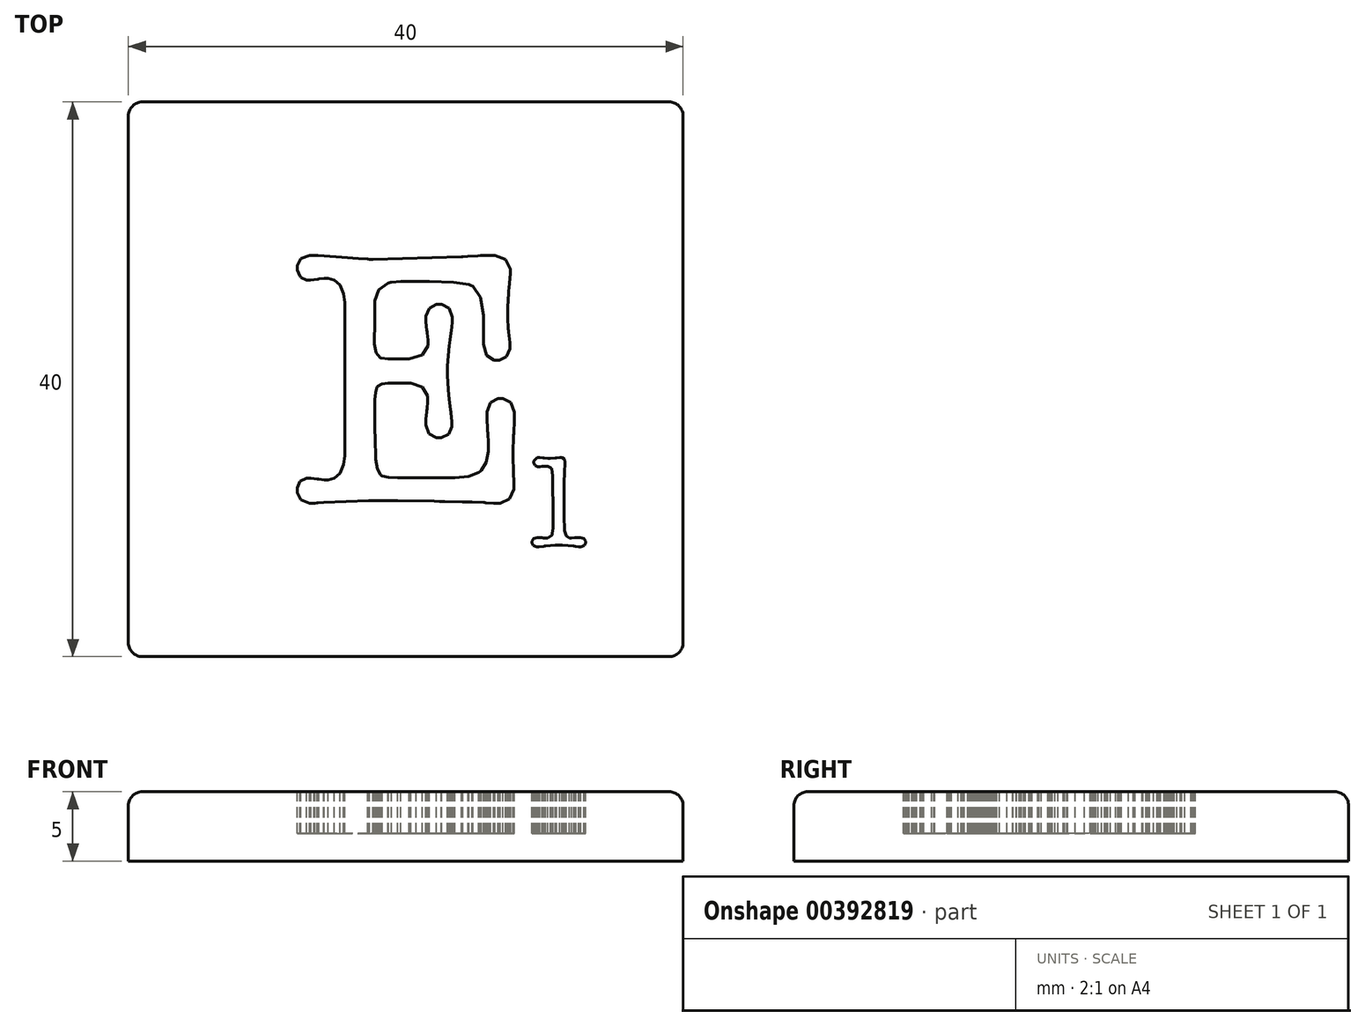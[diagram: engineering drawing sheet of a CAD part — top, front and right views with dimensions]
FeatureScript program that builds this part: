
annotation { "Feature Type Name" : "Feature", "Feature Type Description" : "" }
export const myFeature = defineFeature(function(context is Context, id is Id, definition is map)
    precondition{}
    {
        {
            var Q0;
            Q0=qCreatedBy(makeId("Top.planeOp"),FACE);
            var sketch = newSketch(context, id + "F0", { "sketchPlane" : qUnion([Q0])});
            skLineSegment(sketch, "E0.bottom", {"start": v(20, -20) * mm, "end": v(-20, -20) * mm});
            skLineSegment(sketch, "E0.top", {"start": v(20, 20) * mm, "end": v(-20, 20) * mm});
            skLineSegment(sketch, "E0.left", {"start": v(20, -20) * mm, "end": v(20, 20) * mm});
            skLineSegment(sketch, "E0.right", {"start": v(-20, -20) * mm, "end": v(-20, 20) * mm});
            skPoint(sketch, "E0.middle", {"position": v(0, 0) * mm});
            skSolve(sketch);
        }
        {
            var Q0;
            Q0=makeQuery(id+"F0.imprint","IMPRINT",FACE,{"disambiguationData":[TD([[makeQuery(id+"F0.imprint","IMPRINT",EDGE,{"derivedFrom":sQuery(id+"F0.wireOp",EDGE,"E0.bottom")}),-1.0]])]});
            extrude(context, id + "F1", {"entities" : qUnion([Q0]), "depth" : -5 * mm});
        }
        {
            var Q0;
            Q0=makeQuery(id+"F1.opExtrude","CAP_FACE",FACE,{"disambiguationData":[OSD([sQuery(id+"F0.wireOp",EDGE,"E0.bottom"),sQuery(id+"F0.wireOp",EDGE,"E0.top"),sQuery(id+"F0.wireOp",EDGE,"E0.left"),sQuery(id+"F0.wireOp",EDGE,"E0.right")])],"isStart":true});
            var Q1;
            Q1=makeQuery(id+"F1.opExtrude","SWEPT_EDGE",EDGE,{"disambiguationData":[OSD([sQuery(id+"F0.wireOp",EDGE,"E0.top"),sQuery(id+"F0.wireOp",EDGE,"E0.right")])]});
            var Q2;
            Q2=makeQuery(id+"F1.opExtrude","SWEPT_EDGE",EDGE,{"disambiguationData":[OSD([sQuery(id+"F0.wireOp",EDGE,"E0.top"),sQuery(id+"F0.wireOp",EDGE,"E0.left")])]});
            var Q3;
            Q3=makeQuery(id+"F1.opExtrude","SWEPT_EDGE",EDGE,{"disambiguationData":[OSD([sQuery(id+"F0.wireOp",EDGE,"E0.bottom"),sQuery(id+"F0.wireOp",EDGE,"E0.right")])]});
            var Q4;
            Q4=makeQuery(id+"F1.opExtrude","SWEPT_EDGE",EDGE,{"disambiguationData":[OSD([sQuery(id+"F0.wireOp",EDGE,"E0.bottom"),sQuery(id+"F0.wireOp",EDGE,"E0.left")])]});
            fillet(context, id + "F2", {"entities" : qUnion([Q0, Q1, Q2, Q3, Q4]), "radius" : 1 * mm, "tangentPropagation" : true, "allowEdgeOverflow" : false});
        }
        {
            var Q0;
            Q0=qCreatedBy(makeId("Top.planeOp"),FACE);
            var sketch = newSketch(context, id + "F3", { "sketchPlane" : qUnion([Q0])});
            skLineSegment(sketch, "E1", {"start": v(-4.4, 5.32) * mm, "end": v(-4.4, 5.53) * mm});
            skLineSegment(sketch, "E2", {"start": v(-4.4, 5.53) * mm, "end": v(-4.48, 6.18) * mm});
            skLineSegment(sketch, "E3", {"start": v(-4.48, 6.18) * mm, "end": v(-4.73, 6.79) * mm});
            skLineSegment(sketch, "E4", {"start": v(-4.73, 6.79) * mm, "end": v(-5.15, 7.16) * mm});
            skLineSegment(sketch, "E5", {"start": v(-5.15, 7.16) * mm, "end": v(-5.6, 7.28) * mm});
            skLineSegment(sketch, "E6", {"start": v(-5.6, 7.28) * mm, "end": v(-5.74, 7.28) * mm});
            skLineSegment(sketch, "E7", {"start": v(-5.74, 7.28) * mm, "end": v(-5.88, 7.28) * mm});
            skLineSegment(sketch, "E8", {"start": v(-5.88, 7.28) * mm, "end": v(-6.27, 7.23) * mm});
            skLineSegment(sketch, "E9", {"start": v(-6.27, 7.23) * mm, "end": v(-6.3, 7.22) * mm});
            skLineSegment(sketch, "E10", {"start": v(-6.3, 7.22) * mm, "end": v(-6.37, 7.21) * mm});
            skLineSegment(sketch, "E11", {"start": v(-6.37, 7.21) * mm, "end": v(-6.85, 7.14) * mm});
            skLineSegment(sketch, "E12", {"start": v(-6.85, 7.14) * mm, "end": v(-7.01, 7.14) * mm});
            skLineSegment(sketch, "E13", {"start": v(-7.01, 7.14) * mm, "end": v(-7.16, 7.14) * mm});
            skLineSegment(sketch, "E14", {"start": v(-7.16, 7.14) * mm, "end": v(-7.55, 7.35) * mm});
            skLineSegment(sketch, "E15", {"start": v(-7.55, 7.35) * mm, "end": v(-7.6, 7.4) * mm});
            skLineSegment(sketch, "E16", {"start": v(-7.6, 7.4) * mm, "end": v(-7.63, 7.44) * mm});
            skLineSegment(sketch, "E17", {"start": v(-7.63, 7.44) * mm, "end": v(-7.83, 7.87) * mm});
            skLineSegment(sketch, "E18", {"start": v(-7.83, 7.87) * mm, "end": v(-7.83, 8.02) * mm});
            skLineSegment(sketch, "E19", {"start": v(-7.83, 8.02) * mm, "end": v(-7.83, 8.2) * mm});
            skLineSegment(sketch, "E20", {"start": v(-7.83, 8.2) * mm, "end": v(-7.55, 8.71) * mm});
            skLineSegment(sketch, "E21", {"start": v(-7.55, 8.71) * mm, "end": v(-6.93, 8.94) * mm});
            skLineSegment(sketch, "E22", {"start": v(-6.93, 8.94) * mm, "end": v(-6.72, 8.94) * mm});
            skLineSegment(sketch, "E23", {"start": v(-6.72, 8.94) * mm, "end": v(-6.62, 8.94) * mm});
            skLineSegment(sketch, "E24", {"start": v(-6.62, 8.94) * mm, "end": v(-6.39, 8.92) * mm});
            skLineSegment(sketch, "E25", {"start": v(-6.39, 8.92) * mm, "end": v(-6.32, 8.92) * mm});
            skLineSegment(sketch, "E26", {"start": v(-6.32, 8.92) * mm, "end": v(-5.9, 8.89) * mm});
            skLineSegment(sketch, "E27", {"start": v(-5.9, 8.89) * mm, "end": v(-4.6, 8.8) * mm});
            skLineSegment(sketch, "E28", {"start": v(-4.6, 8.8) * mm, "end": v(-3.41, 8.72) * mm});
            skLineSegment(sketch, "E29", {"start": v(-3.41, 8.72) * mm, "end": v(-2.75, 8.67) * mm});
            skLineSegment(sketch, "E30", {"start": v(-2.75, 8.67) * mm, "end": v(-2.62, 8.65) * mm});
            skLineSegment(sketch, "E31", {"start": v(-2.62, 8.65) * mm, "end": v(-2.36, 8.65) * mm});
            skLineSegment(sketch, "E32", {"start": v(-2.36, 8.65) * mm, "end": v(4.02, 8.84) * mm});
            skLineSegment(sketch, "E33", {"start": v(4.02, 8.84) * mm, "end": v(4.13, 8.84) * mm});
            skLineSegment(sketch, "E34", {"start": v(4.13, 8.84) * mm, "end": v(4.46, 8.86) * mm});
            skLineSegment(sketch, "E35", {"start": v(4.46, 8.86) * mm, "end": v(5.2, 8.9) * mm});
            skLineSegment(sketch, "E36", {"start": v(5.2, 8.9) * mm, "end": v(5.4, 8.92) * mm});
            skLineSegment(sketch, "E37", {"start": v(5.4, 8.92) * mm, "end": v(5.47, 8.92) * mm});
            skLineSegment(sketch, "E38", {"start": v(5.47, 8.92) * mm, "end": v(6, 8.94) * mm});
            skLineSegment(sketch, "E39", {"start": v(6, 8.94) * mm, "end": v(6.17, 8.94) * mm});
            skLineSegment(sketch, "E40", {"start": v(6.17, 8.94) * mm, "end": v(6.42, 8.94) * mm});
            skLineSegment(sketch, "E41", {"start": v(6.42, 8.94) * mm, "end": v(7.2, 8.64) * mm});
            skLineSegment(sketch, "E42", {"start": v(7.2, 8.64) * mm, "end": v(7.54, 7.95) * mm});
            skLineSegment(sketch, "E43", {"start": v(7.54, 7.95) * mm, "end": v(7.54, 7.73) * mm});
            skLineSegment(sketch, "E44", {"start": v(7.54, 7.73) * mm, "end": v(7.54, 7.62) * mm});
            skLineSegment(sketch, "E45", {"start": v(7.54, 7.62) * mm, "end": v(7.51, 7.28) * mm});
            skLineSegment(sketch, "E46", {"start": v(7.51, 7.28) * mm, "end": v(7.45, 6.57) * mm});
            skLineSegment(sketch, "E47", {"start": v(7.45, 6.57) * mm, "end": v(7.43, 6.38) * mm});
            skLineSegment(sketch, "E48", {"start": v(7.43, 6.38) * mm, "end": v(7.42, 6.24) * mm});
            skLineSegment(sketch, "E49", {"start": v(7.42, 6.24) * mm, "end": v(7.36, 5.17) * mm});
            skLineSegment(sketch, "E50", {"start": v(7.36, 5.17) * mm, "end": v(7.36, 4.82) * mm});
            skLineSegment(sketch, "E51", {"start": v(7.36, 4.82) * mm, "end": v(7.36, 4.5) * mm});
            skLineSegment(sketch, "E52", {"start": v(7.36, 4.5) * mm, "end": v(7.4, 3.58) * mm});
            skLineSegment(sketch, "E53", {"start": v(7.4, 3.58) * mm, "end": v(7.4, 3.52) * mm});
            skLineSegment(sketch, "E54", {"start": v(7.4, 3.52) * mm, "end": v(7.42, 3.4) * mm});
            skLineSegment(sketch, "E55", {"start": v(7.42, 3.4) * mm, "end": v(7.51, 2.64) * mm});
            skLineSegment(sketch, "E56", {"start": v(7.51, 2.64) * mm, "end": v(7.51, 2.38) * mm});
            skLineSegment(sketch, "E57", {"start": v(7.51, 2.38) * mm, "end": v(7.51, 2.2) * mm});
            skLineSegment(sketch, "E58", {"start": v(7.51, 2.2) * mm, "end": v(7.28, 1.63) * mm});
            skLineSegment(sketch, "E59", {"start": v(7.28, 1.63) * mm, "end": v(6.74, 1.38) * mm});
            skLineSegment(sketch, "E60", {"start": v(6.74, 1.38) * mm, "end": v(6.56, 1.38) * mm});
            skLineSegment(sketch, "E61", {"start": v(6.56, 1.38) * mm, "end": v(6.38, 1.38) * mm});
            skLineSegment(sketch, "E62", {"start": v(6.38, 1.38) * mm, "end": v(5.85, 1.73) * mm});
            skLineSegment(sketch, "E63", {"start": v(5.85, 1.73) * mm, "end": v(5.6, 2.52) * mm});
            skLineSegment(sketch, "E64", {"start": v(5.6, 2.52) * mm, "end": v(5.6, 2.78) * mm});
            skLineSegment(sketch, "E65", {"start": v(5.6, 2.78) * mm, "end": v(5.6, 4.15) * mm});
            skLineSegment(sketch, "E66", {"start": v(5.6, 4.15) * mm, "end": v(5.6, 4.6) * mm});
            skLineSegment(sketch, "E67", {"start": v(5.6, 4.6) * mm, "end": v(5.38, 5.92) * mm});
            skLineSegment(sketch, "E68", {"start": v(5.38, 5.92) * mm, "end": v(4.84, 6.7) * mm});
            skLineSegment(sketch, "E69", {"start": v(4.84, 6.7) * mm, "end": v(4.68, 6.77) * mm});
            skLineSegment(sketch, "E70", {"start": v(4.68, 6.77) * mm, "end": v(4.57, 6.82) * mm});
            skLineSegment(sketch, "E71", {"start": v(4.57, 6.82) * mm, "end": v(3.45, 7) * mm});
            skLineSegment(sketch, "E72", {"start": v(3.45, 7) * mm, "end": v(1.72, 7.06) * mm});
            skLineSegment(sketch, "E73", {"start": v(1.72, 7.06) * mm, "end": v(1.14, 7.06) * mm});
            skLineSegment(sketch, "E74", {"start": v(1.14, 7.06) * mm, "end": v(0.76, 7.06) * mm});
            skLineSegment(sketch, "E75", {"start": v(0.76, 7.06) * mm, "end": v(-0.36, 7.05) * mm});
            skLineSegment(sketch, "E76", {"start": v(-0.36, 7.05) * mm, "end": v(-1.03, 7) * mm});
            skLineSegment(sketch, "E77", {"start": v(-1.03, 7) * mm, "end": v(-1.08, 6.98) * mm});
            skLineSegment(sketch, "E78", {"start": v(-1.08, 6.98) * mm, "end": v(-1.27, 6.94) * mm});
            skLineSegment(sketch, "E79", {"start": v(-1.27, 6.94) * mm, "end": v(-1.94, 6.44) * mm});
            skLineSegment(sketch, "E80", {"start": v(-1.94, 6.44) * mm, "end": v(-2.22, 5.66) * mm});
            skLineSegment(sketch, "E81", {"start": v(-2.22, 5.66) * mm, "end": v(-2.22, 5.4) * mm});
            skLineSegment(sketch, "E82", {"start": v(-2.22, 5.4) * mm, "end": v(-2.22, 3.62) * mm});
            skLineSegment(sketch, "E83", {"start": v(-2.22, 3.62) * mm, "end": v(-2.23, 3.56) * mm});
            skLineSegment(sketch, "E84", {"start": v(-2.23, 3.56) * mm, "end": v(-2.25, 3.21) * mm});
            skLineSegment(sketch, "E85", {"start": v(-2.25, 3.21) * mm, "end": v(-2.25, 3.1) * mm});
            skLineSegment(sketch, "E86", {"start": v(-2.25, 3.1) * mm, "end": v(-2.25, 2.75) * mm});
            skLineSegment(sketch, "E87", {"start": v(-2.25, 2.75) * mm, "end": v(-2.25, 2.54) * mm});
            skLineSegment(sketch, "E88", {"start": v(-2.25, 2.54) * mm, "end": v(-2.13, 1.92) * mm});
            skLineSegment(sketch, "E89", {"start": v(-2.13, 1.92) * mm, "end": v(-1.85, 1.56) * mm});
            skLineSegment(sketch, "E90", {"start": v(-1.85, 1.56) * mm, "end": v(-1.77, 1.53) * mm});
            skLineSegment(sketch, "E91", {"start": v(-1.77, 1.53) * mm, "end": v(-1.74, 1.53) * mm});
            skLineSegment(sketch, "E92", {"start": v(-1.74, 1.53) * mm, "end": v(-1.29, 1.48) * mm});
            skLineSegment(sketch, "E93", {"start": v(-1.29, 1.48) * mm, "end": v(-1.14, 1.48) * mm});
            skLineSegment(sketch, "E94", {"start": v(-1.14, 1.48) * mm, "end": v(-0.05, 1.48) * mm});
            skLineSegment(sketch, "E95", {"start": v(-0.05, 1.48) * mm, "end": v(0.26, 1.48) * mm});
            skLineSegment(sketch, "E96", {"start": v(0.26, 1.48) * mm, "end": v(1.2, 1.77) * mm});
            skLineSegment(sketch, "E97", {"start": v(1.2, 1.77) * mm, "end": v(1.61, 2.4) * mm});
            skLineSegment(sketch, "E98", {"start": v(1.61, 2.4) * mm, "end": v(1.61, 2.62) * mm});
            skLineSegment(sketch, "E99", {"start": v(1.61, 2.62) * mm, "end": v(1.61, 2.82) * mm});
            skLineSegment(sketch, "E100", {"start": v(1.61, 2.82) * mm, "end": v(1.55, 3.36) * mm});
            skLineSegment(sketch, "E101", {"start": v(1.55, 3.36) * mm, "end": v(1.54, 3.44) * mm});
            skLineSegment(sketch, "E102", {"start": v(1.54, 3.44) * mm, "end": v(1.52, 3.52) * mm});
            skLineSegment(sketch, "E103", {"start": v(1.52, 3.52) * mm, "end": v(1.46, 4.14) * mm});
            skLineSegment(sketch, "E104", {"start": v(1.46, 4.14) * mm, "end": v(1.46, 4.34) * mm});
            skLineSegment(sketch, "E105", {"start": v(1.46, 4.34) * mm, "end": v(1.46, 4.54) * mm});
            skLineSegment(sketch, "E106", {"start": v(1.46, 4.54) * mm, "end": v(1.7, 5.13) * mm});
            skLineSegment(sketch, "E107", {"start": v(1.7, 5.13) * mm, "end": v(2.23, 5.4) * mm});
            skLineSegment(sketch, "E108", {"start": v(2.23, 5.4) * mm, "end": v(2.4, 5.4) * mm});
            skLineSegment(sketch, "E109", {"start": v(2.4, 5.4) * mm, "end": v(2.59, 5.4) * mm});
            skLineSegment(sketch, "E110", {"start": v(2.59, 5.4) * mm, "end": v(3.12, 5.11) * mm});
            skLineSegment(sketch, "E111", {"start": v(3.12, 5.11) * mm, "end": v(3.36, 4.47) * mm});
            skLineSegment(sketch, "E112", {"start": v(3.36, 4.47) * mm, "end": v(3.36, 4.26) * mm});
            skLineSegment(sketch, "E113", {"start": v(3.36, 4.26) * mm, "end": v(3.36, 4.13) * mm});
            skLineSegment(sketch, "E114", {"start": v(3.36, 4.13) * mm, "end": v(3.31, 3.74) * mm});
            skLineSegment(sketch, "E115", {"start": v(3.31, 3.74) * mm, "end": v(3.2, 2.86) * mm});
            skLineSegment(sketch, "E116", {"start": v(3.2, 2.86) * mm, "end": v(3.18, 2.62) * mm});
            skLineSegment(sketch, "E117", {"start": v(3.18, 2.62) * mm, "end": v(3.15, 2.42) * mm});
            skLineSegment(sketch, "E118", {"start": v(3.15, 2.42) * mm, "end": v(3.02, 0.96) * mm});
            skLineSegment(sketch, "E119", {"start": v(3.02, 0.96) * mm, "end": v(3.02, 0.48) * mm});
            skLineSegment(sketch, "E120", {"start": v(3.02, 0.48) * mm, "end": v(3.02, 0.3) * mm});
            skLineSegment(sketch, "E121", {"start": v(3.02, 0.3) * mm, "end": v(3.04, -0.26) * mm});
            skLineSegment(sketch, "E122", {"start": v(3.04, -0.26) * mm, "end": v(3.1, -1.18) * mm});
            skLineSegment(sketch, "E123", {"start": v(3.1, -1.18) * mm, "end": v(3.12, -1.4) * mm});
            skLineSegment(sketch, "E124", {"start": v(3.12, -1.4) * mm, "end": v(3.13, -1.44) * mm});
            skLineSegment(sketch, "E125", {"start": v(3.13, -1.44) * mm, "end": v(3.24, -2.2) * mm});
            skLineSegment(sketch, "E126", {"start": v(3.24, -2.2) * mm, "end": v(3.25, -2.33) * mm});
            skLineSegment(sketch, "E127", {"start": v(3.25, -2.33) * mm, "end": v(3.27, -2.42) * mm});
            skLineSegment(sketch, "E128", {"start": v(3.27, -2.42) * mm, "end": v(3.33, -3.05) * mm});
            skLineSegment(sketch, "E129", {"start": v(3.33, -3.05) * mm, "end": v(3.33, -3.25) * mm});
            skLineSegment(sketch, "E130", {"start": v(3.33, -3.25) * mm, "end": v(3.33, -3.43) * mm});
            skLineSegment(sketch, "E131", {"start": v(3.33, -3.43) * mm, "end": v(3.1, -3.97) * mm});
            skLineSegment(sketch, "E132", {"start": v(3.1, -3.97) * mm, "end": v(2.56, -4.2) * mm});
            skLineSegment(sketch, "E133", {"start": v(2.56, -4.2) * mm, "end": v(2.38, -4.2) * mm});
            skLineSegment(sketch, "E134", {"start": v(2.38, -4.2) * mm, "end": v(2.2, -4.2) * mm});
            skLineSegment(sketch, "E135", {"start": v(2.2, -4.2) * mm, "end": v(1.69, -3.93) * mm});
            skLineSegment(sketch, "E136", {"start": v(1.69, -3.93) * mm, "end": v(1.46, -3.3) * mm});
            skLineSegment(sketch, "E137", {"start": v(1.46, -3.3) * mm, "end": v(1.46, -3.1) * mm});
            skLineSegment(sketch, "E138", {"start": v(1.46, -3.1) * mm, "end": v(1.46, -2.88) * mm});
            skLineSegment(sketch, "E139", {"start": v(1.46, -2.88) * mm, "end": v(1.51, -2.34) * mm});
            skLineSegment(sketch, "E140", {"start": v(1.51, -2.34) * mm, "end": v(1.52, -2.25) * mm});
            skLineSegment(sketch, "E141", {"start": v(1.52, -2.25) * mm, "end": v(1.53, -2.16) * mm});
            skLineSegment(sketch, "E142", {"start": v(1.53, -2.16) * mm, "end": v(1.59, -1.59) * mm});
            skLineSegment(sketch, "E143", {"start": v(1.59, -1.59) * mm, "end": v(1.59, -1.4) * mm});
            skLineSegment(sketch, "E144", {"start": v(1.59, -1.4) * mm, "end": v(1.59, -1.19) * mm});
            skLineSegment(sketch, "E145", {"start": v(1.59, -1.19) * mm, "end": v(1.2, -0.55) * mm});
            skLineSegment(sketch, "E146", {"start": v(1.2, -0.55) * mm, "end": v(0.36, -0.26) * mm});
            skLineSegment(sketch, "E147", {"start": v(0.36, -0.26) * mm, "end": v(0.08, -0.26) * mm});
            skLineSegment(sketch, "E148", {"start": v(0.08, -0.26) * mm, "end": v(-1.11, -0.26) * mm});
            skLineSegment(sketch, "E149", {"start": v(-1.11, -0.26) * mm, "end": v(-1.27, -0.26) * mm});
            skLineSegment(sketch, "E150", {"start": v(-1.27, -0.26) * mm, "end": v(-1.73, -0.33) * mm});
            skLineSegment(sketch, "E151", {"start": v(-1.73, -0.33) * mm, "end": v(-2.02, -0.48) * mm});
            skLineSegment(sketch, "E152", {"start": v(-2.02, -0.48) * mm, "end": v(-2.05, -0.53) * mm});
            skLineSegment(sketch, "E153", {"start": v(-2.05, -0.53) * mm, "end": v(-2.08, -0.57) * mm});
            skLineSegment(sketch, "E154", {"start": v(-2.08, -0.57) * mm, "end": v(-2.18, -0.94) * mm});
            skLineSegment(sketch, "E155", {"start": v(-2.18, -0.94) * mm, "end": v(-2.22, -1.49) * mm});
            skLineSegment(sketch, "E156", {"start": v(-2.22, -1.49) * mm, "end": v(-2.22, -1.67) * mm});
            skLineSegment(sketch, "E157", {"start": v(-2.22, -1.67) * mm, "end": v(-2.22, -3.3) * mm});
            skLineSegment(sketch, "E158", {"start": v(-2.22, -3.3) * mm, "end": v(-2.22, -3.6) * mm});
            skLineSegment(sketch, "E159", {"start": v(-2.22, -3.6) * mm, "end": v(-2.2, -4.32) * mm});
            skLineSegment(sketch, "E160", {"start": v(-2.2, -4.32) * mm, "end": v(-2.2, -4.44) * mm});
            skLineSegment(sketch, "E161", {"start": v(-2.2, -4.44) * mm, "end": v(-2.2, -4.59) * mm});
            skLineSegment(sketch, "E162", {"start": v(-2.2, -4.59) * mm, "end": v(-2.17, -5.35) * mm});
            skLineSegment(sketch, "E163", {"start": v(-2.17, -5.35) * mm, "end": v(-2.17, -5.6) * mm});
            skLineSegment(sketch, "E164", {"start": v(-2.17, -5.6) * mm, "end": v(-2.16, -5.79) * mm});
            skLineSegment(sketch, "E165", {"start": v(-2.16, -5.79) * mm, "end": v(-2.05, -6.47) * mm});
            skLineSegment(sketch, "E166", {"start": v(-2.05, -6.47) * mm, "end": v(-1.81, -6.89) * mm});
            skLineSegment(sketch, "E167", {"start": v(-1.81, -6.89) * mm, "end": v(-1.75, -6.93) * mm});
            skLineSegment(sketch, "E168", {"start": v(-1.75, -6.93) * mm, "end": v(-1.7, -6.96) * mm});
            skLineSegment(sketch, "E169", {"start": v(-1.7, -6.96) * mm, "end": v(-1.26, -7.07) * mm});
            skLineSegment(sketch, "E170", {"start": v(-1.26, -7.07) * mm, "end": v(-0.6, -7.12) * mm});
            skLineSegment(sketch, "E171", {"start": v(-0.6, -7.12) * mm, "end": v(-0.37, -7.12) * mm});
            skLineSegment(sketch, "E172", {"start": v(-0.37, -7.12) * mm, "end": v(3.23, -7.12) * mm});
            skLineSegment(sketch, "E173", {"start": v(3.23, -7.12) * mm, "end": v(3.56, -7.12) * mm});
            skLineSegment(sketch, "E174", {"start": v(3.56, -7.12) * mm, "end": v(4.54, -7) * mm});
            skLineSegment(sketch, "E175", {"start": v(4.54, -7) * mm, "end": v(5.27, -6.73) * mm});
            skLineSegment(sketch, "E176", {"start": v(5.27, -6.73) * mm, "end": v(5.37, -6.65) * mm});
            skLineSegment(sketch, "E177", {"start": v(5.37, -6.65) * mm, "end": v(5.47, -6.58) * mm});
            skLineSegment(sketch, "E178", {"start": v(5.47, -6.58) * mm, "end": v(5.8, -5.99) * mm});
            skLineSegment(sketch, "E179", {"start": v(5.8, -5.99) * mm, "end": v(5.95, -5.19) * mm});
            skLineSegment(sketch, "E180", {"start": v(5.95, -5.19) * mm, "end": v(5.95, -4.92) * mm});
            skLineSegment(sketch, "E181", {"start": v(5.95, -4.92) * mm, "end": v(5.95, -4.63) * mm});
            skLineSegment(sketch, "E182", {"start": v(5.95, -4.63) * mm, "end": v(5.92, -3.87) * mm});
            skLineSegment(sketch, "E183", {"start": v(5.92, -3.87) * mm, "end": v(5.91, -3.74) * mm});
            skLineSegment(sketch, "E184", {"start": v(5.91, -3.74) * mm, "end": v(5.9, -3.61) * mm});
            skLineSegment(sketch, "E185", {"start": v(5.9, -3.61) * mm, "end": v(5.87, -2.83) * mm});
            skLineSegment(sketch, "E186", {"start": v(5.87, -2.83) * mm, "end": v(5.87, -2.57) * mm});
            skLineSegment(sketch, "E187", {"start": v(5.87, -2.57) * mm, "end": v(5.87, -2.34) * mm});
            skLineSegment(sketch, "E188", {"start": v(5.87, -2.34) * mm, "end": v(6.11, -1.67) * mm});
            skLineSegment(sketch, "E189", {"start": v(6.11, -1.67) * mm, "end": v(6.65, -1.38) * mm});
            skLineSegment(sketch, "E190", {"start": v(6.65, -1.38) * mm, "end": v(6.83, -1.38) * mm});
            skLineSegment(sketch, "E191", {"start": v(6.83, -1.38) * mm, "end": v(7.01, -1.38) * mm});
            skLineSegment(sketch, "E192", {"start": v(7.01, -1.38) * mm, "end": v(7.58, -1.68) * mm});
            skLineSegment(sketch, "E193", {"start": v(7.58, -1.68) * mm, "end": v(7.83, -2.36) * mm});
            skLineSegment(sketch, "E194", {"start": v(7.83, -2.36) * mm, "end": v(7.83, -2.6) * mm});
            skLineSegment(sketch, "E195", {"start": v(7.83, -2.6) * mm, "end": v(7.83, -2.96) * mm});
            skLineSegment(sketch, "E196", {"start": v(7.83, -2.96) * mm, "end": v(7.79, -3.88) * mm});
            skLineSegment(sketch, "E197", {"start": v(7.79, -3.88) * mm, "end": v(7.78, -4.05) * mm});
            skLineSegment(sketch, "E198", {"start": v(7.78, -4.05) * mm, "end": v(7.77, -4.21) * mm});
            skLineSegment(sketch, "E199", {"start": v(7.77, -4.21) * mm, "end": v(7.73, -5.18) * mm});
            skLineSegment(sketch, "E200", {"start": v(7.73, -5.18) * mm, "end": v(7.73, -5.5) * mm});
            skLineSegment(sketch, "E201", {"start": v(7.73, -5.5) * mm, "end": v(7.73, -5.78) * mm});
            skLineSegment(sketch, "E202", {"start": v(7.73, -5.78) * mm, "end": v(7.76, -6.48) * mm});
            skLineSegment(sketch, "E203", {"start": v(7.76, -6.48) * mm, "end": v(7.77, -6.6) * mm});
            skLineSegment(sketch, "E204", {"start": v(7.77, -6.6) * mm, "end": v(7.77, -6.72) * mm});
            skLineSegment(sketch, "E205", {"start": v(7.77, -6.72) * mm, "end": v(7.8, -7.45) * mm});
            skLineSegment(sketch, "E206", {"start": v(7.8, -7.45) * mm, "end": v(7.8, -7.7) * mm});
            skLineSegment(sketch, "E207", {"start": v(7.8, -7.7) * mm, "end": v(7.8, -7.93) * mm});
            skLineSegment(sketch, "E208", {"start": v(7.8, -7.93) * mm, "end": v(7.5, -8.63) * mm});
            skLineSegment(sketch, "E209", {"start": v(7.5, -8.63) * mm, "end": v(6.82, -8.94) * mm});
            skLineSegment(sketch, "E210", {"start": v(6.82, -8.94) * mm, "end": v(6.59, -8.94) * mm});
            skLineSegment(sketch, "E211", {"start": v(6.59, -8.94) * mm, "end": v(6.36, -8.94) * mm});
            skLineSegment(sketch, "E212", {"start": v(6.36, -8.94) * mm, "end": v(5.77, -8.9) * mm});
            skLineSegment(sketch, "E213", {"start": v(5.77, -8.9) * mm, "end": v(5.66, -8.9) * mm});
            skLineSegment(sketch, "E214", {"start": v(5.66, -8.9) * mm, "end": v(5.6, -8.88) * mm});
            skLineSegment(sketch, "E215", {"start": v(5.6, -8.88) * mm, "end": v(4.77, -8.86) * mm});
            skLineSegment(sketch, "E216", {"start": v(4.77, -8.86) * mm, "end": v(4.5, -8.86) * mm});
            skLineSegment(sketch, "E217", {"start": v(4.5, -8.86) * mm, "end": v(4.07, -8.85) * mm});
            skLineSegment(sketch, "E218", {"start": v(4.07, -8.85) * mm, "end": v(2.8, -8.82) * mm});
            skLineSegment(sketch, "E219", {"start": v(2.8, -8.82) * mm, "end": v(2.43, -8.81) * mm});
            skLineSegment(sketch, "E220", {"start": v(2.43, -8.81) * mm, "end": v(2.06, -8.8) * mm});
            skLineSegment(sketch, "E221", {"start": v(2.06, -8.8) * mm, "end": v(-0.58, -8.76) * mm});
            skLineSegment(sketch, "E222", {"start": v(-0.58, -8.76) * mm, "end": v(-1.46, -8.76) * mm});
            skLineSegment(sketch, "E223", {"start": v(-1.46, -8.76) * mm, "end": v(-2.67, -8.76) * mm});
            skLineSegment(sketch, "E224", {"start": v(-2.67, -8.76) * mm, "end": v(-5.93, -8.89) * mm});
            skLineSegment(sketch, "E225", {"start": v(-5.93, -8.89) * mm, "end": v(-6.32, -8.92) * mm});
            skLineSegment(sketch, "E226", {"start": v(-6.32, -8.92) * mm, "end": v(-6.38, -8.92) * mm});
            skLineSegment(sketch, "E227", {"start": v(-6.38, -8.92) * mm, "end": v(-6.54, -8.94) * mm});
            skLineSegment(sketch, "E228", {"start": v(-6.54, -8.94) * mm, "end": v(-6.56, -8.94) * mm});
            skLineSegment(sketch, "E229", {"start": v(-6.56, -8.94) * mm, "end": v(-6.72, -8.94) * mm});
            skLineSegment(sketch, "E230", {"start": v(-6.72, -8.94) * mm, "end": v(-6.93, -8.94) * mm});
            skLineSegment(sketch, "E231", {"start": v(-6.93, -8.94) * mm, "end": v(-7.55, -8.7) * mm});
            skLineSegment(sketch, "E232", {"start": v(-7.55, -8.7) * mm, "end": v(-7.83, -8.17) * mm});
            skLineSegment(sketch, "E233", {"start": v(-7.83, -8.17) * mm, "end": v(-7.83, -8) * mm});
            skLineSegment(sketch, "E234", {"start": v(-7.83, -8) * mm, "end": v(-7.83, -7.83) * mm});
            skLineSegment(sketch, "E235", {"start": v(-7.83, -7.83) * mm, "end": v(-7.63, -7.35) * mm});
            skLineSegment(sketch, "E236", {"start": v(-7.63, -7.35) * mm, "end": v(-7.17, -7.14) * mm});
            skLineSegment(sketch, "E237", {"start": v(-7.17, -7.14) * mm, "end": v(-7.01, -7.14) * mm});
            skLineSegment(sketch, "E238", {"start": v(-7.01, -7.14) * mm, "end": v(-6.83, -7.14) * mm});
            skLineSegment(sketch, "E239", {"start": v(-6.83, -7.14) * mm, "end": v(-6.4, -7.19) * mm});
            skLineSegment(sketch, "E240", {"start": v(-6.4, -7.19) * mm, "end": v(-6.3, -7.2) * mm});
            skLineSegment(sketch, "E241", {"start": v(-6.3, -7.2) * mm, "end": v(-6.25, -7.2) * mm});
            skLineSegment(sketch, "E242", {"start": v(-6.25, -7.2) * mm, "end": v(-5.87, -7.28) * mm});
            skLineSegment(sketch, "E243", {"start": v(-5.87, -7.28) * mm, "end": v(-5.74, -7.28) * mm});
            skLineSegment(sketch, "E244", {"start": v(-5.74, -7.28) * mm, "end": v(-5.6, -7.28) * mm});
            skLineSegment(sketch, "E245", {"start": v(-5.6, -7.28) * mm, "end": v(-5.15, -7.15) * mm});
            skLineSegment(sketch, "E246", {"start": v(-5.15, -7.15) * mm, "end": v(-4.73, -6.78) * mm});
            skLineSegment(sketch, "E247", {"start": v(-4.73, -6.78) * mm, "end": v(-4.48, -6.16) * mm});
            skLineSegment(sketch, "E248", {"start": v(-4.48, -6.16) * mm, "end": v(-4.4, -5.5) * mm});
            skLineSegment(sketch, "E249", {"start": v(-4.4, -5.5) * mm, "end": v(-4.4, -5.3) * mm});
            skLineSegment(sketch, "E250", {"start": v(-4.4, -5.3) * mm, "end": v(-4.4, 5.32) * mm});
            skSolve(sketch);
        }
        {
            var Q0;
            Q0=qCreatedBy(makeId("Top.planeOp"),FACE);
            var sketch = newSketch(context, id + "F4", { "sketchPlane" : qUnion([Q0])});
            skLineSegment(sketch, "E251", {"start": v(10.64, -9.84) * mm, "end": v(10.61, -7.07) * mm});
            skLineSegment(sketch, "E252", {"start": v(10.61, -7.07) * mm, "end": v(10.61, -7) * mm});
            skLineSegment(sketch, "E253", {"start": v(10.61, -7) * mm, "end": v(10.53, -6.45) * mm});
            skLineSegment(sketch, "E254", {"start": v(10.53, -6.45) * mm, "end": v(10.51, -6.43) * mm});
            skLineSegment(sketch, "E255", {"start": v(10.51, -6.43) * mm, "end": v(10.5, -6.4) * mm});
            skLineSegment(sketch, "E256", {"start": v(10.5, -6.4) * mm, "end": v(10.24, -6.26) * mm});
            skLineSegment(sketch, "E257", {"start": v(10.24, -6.26) * mm, "end": v(10.16, -6.26) * mm});
            skLineSegment(sketch, "E258", {"start": v(10.16, -6.26) * mm, "end": v(10.09, -6.26) * mm});
            skLineSegment(sketch, "E259", {"start": v(10.09, -6.26) * mm, "end": v(9.9, -6.28) * mm});
            skLineSegment(sketch, "E260", {"start": v(9.9, -6.28) * mm, "end": v(9.88, -6.29) * mm});
            skLineSegment(sketch, "E261", {"start": v(9.88, -6.29) * mm, "end": v(9.85, -6.3) * mm});
            skLineSegment(sketch, "E262", {"start": v(9.85, -6.3) * mm, "end": v(9.66, -6.31) * mm});
            skLineSegment(sketch, "E263", {"start": v(9.66, -6.31) * mm, "end": v(9.6, -6.31) * mm});
            skLineSegment(sketch, "E264", {"start": v(9.6, -6.31) * mm, "end": v(9.53, -6.31) * mm});
            skLineSegment(sketch, "E265", {"start": v(9.53, -6.31) * mm, "end": v(9.32, -6.23) * mm});
            skLineSegment(sketch, "E266", {"start": v(9.32, -6.23) * mm, "end": v(9.23, -6.04) * mm});
            skLineSegment(sketch, "E267", {"start": v(9.23, -6.04) * mm, "end": v(9.23, -5.98) * mm});
            skLineSegment(sketch, "E268", {"start": v(9.23, -5.98) * mm, "end": v(9.23, -5.9) * mm});
            skLineSegment(sketch, "E269", {"start": v(9.23, -5.9) * mm, "end": v(9.5, -5.64) * mm});
            skLineSegment(sketch, "E270", {"start": v(9.5, -5.64) * mm, "end": v(9.58, -5.64) * mm});
            skLineSegment(sketch, "E271", {"start": v(9.58, -5.64) * mm, "end": v(9.67, -5.64) * mm});
            skLineSegment(sketch, "E272", {"start": v(9.67, -5.64) * mm, "end": v(9.9, -5.66) * mm});
            skLineSegment(sketch, "E273", {"start": v(9.9, -5.66) * mm, "end": v(9.94, -5.67) * mm});
            skLineSegment(sketch, "E274", {"start": v(9.94, -5.67) * mm, "end": v(9.98, -5.67) * mm});
            skLineSegment(sketch, "E275", {"start": v(9.98, -5.67) * mm, "end": v(10.23, -5.7) * mm});
            skLineSegment(sketch, "E276", {"start": v(10.23, -5.7) * mm, "end": v(10.32, -5.7) * mm});
            skLineSegment(sketch, "E277", {"start": v(10.32, -5.7) * mm, "end": v(10.44, -5.7) * mm});
            skLineSegment(sketch, "E278", {"start": v(10.44, -5.7) * mm, "end": v(10.79, -5.68) * mm});
            skLineSegment(sketch, "E279", {"start": v(10.79, -5.68) * mm, "end": v(10.82, -5.67) * mm});
            skLineSegment(sketch, "E280", {"start": v(10.82, -5.67) * mm, "end": v(10.87, -5.67) * mm});
            skLineSegment(sketch, "E281", {"start": v(10.87, -5.67) * mm, "end": v(11.1, -5.64) * mm});
            skLineSegment(sketch, "E282", {"start": v(11.1, -5.64) * mm, "end": v(11.18, -5.64) * mm});
            skLineSegment(sketch, "E283", {"start": v(11.18, -5.64) * mm, "end": v(11.25, -5.64) * mm});
            skLineSegment(sketch, "E284", {"start": v(11.25, -5.64) * mm, "end": v(11.43, -5.75) * mm});
            skLineSegment(sketch, "E285", {"start": v(11.43, -5.75) * mm, "end": v(11.44, -5.77) * mm});
            skLineSegment(sketch, "E286", {"start": v(11.44, -5.77) * mm, "end": v(11.45, -5.78) * mm});
            skLineSegment(sketch, "E287", {"start": v(11.45, -5.78) * mm, "end": v(11.48, -6) * mm});
            skLineSegment(sketch, "E288", {"start": v(11.48, -6) * mm, "end": v(11.48, -6.06) * mm});
            skLineSegment(sketch, "E289", {"start": v(11.48, -6.06) * mm, "end": v(11.48, -6.12) * mm});
            skLineSegment(sketch, "E290", {"start": v(11.48, -6.12) * mm, "end": v(11.47, -6.26) * mm});
            skLineSegment(sketch, "E291", {"start": v(11.47, -6.26) * mm, "end": v(11.47, -6.3) * mm});
            skLineSegment(sketch, "E292", {"start": v(11.47, -6.3) * mm, "end": v(11.46, -6.46) * mm});
            skLineSegment(sketch, "E293", {"start": v(11.46, -6.46) * mm, "end": v(11.42, -7.72) * mm});
            skLineSegment(sketch, "E294", {"start": v(11.42, -7.72) * mm, "end": v(11.42, -8.14) * mm});
            skLineSegment(sketch, "E295", {"start": v(11.42, -8.14) * mm, "end": v(11.42, -9.22) * mm});
            skLineSegment(sketch, "E296", {"start": v(11.42, -9.22) * mm, "end": v(11.43, -9.92) * mm});
            skLineSegment(sketch, "E297", {"start": v(11.43, -9.92) * mm, "end": v(11.43, -10) * mm});
            skLineSegment(sketch, "E298", {"start": v(11.43, -10) * mm, "end": v(11.43, -10.1) * mm});
            skLineSegment(sketch, "E299", {"start": v(11.43, -10.1) * mm, "end": v(11.45, -10.62) * mm});
            skLineSegment(sketch, "E300", {"start": v(11.45, -10.62) * mm, "end": v(11.45, -10.8) * mm});
            skLineSegment(sketch, "E301", {"start": v(11.45, -10.8) * mm, "end": v(11.45, -10.9) * mm});
            skLineSegment(sketch, "E302", {"start": v(11.45, -10.9) * mm, "end": v(11.56, -11.29) * mm});
            skLineSegment(sketch, "E303", {"start": v(11.56, -11.29) * mm, "end": v(11.8, -11.45) * mm});
            skLineSegment(sketch, "E304", {"start": v(11.8, -11.45) * mm, "end": v(11.89, -11.45) * mm});
            skLineSegment(sketch, "E305", {"start": v(11.89, -11.45) * mm, "end": v(11.97, -11.45) * mm});
            skLineSegment(sketch, "E306", {"start": v(11.97, -11.45) * mm, "end": v(12.17, -11.43) * mm});
            skLineSegment(sketch, "E307", {"start": v(12.17, -11.43) * mm, "end": v(12.2, -11.43) * mm});
            skLineSegment(sketch, "E308", {"start": v(12.2, -11.43) * mm, "end": v(12.24, -11.43) * mm});
            skLineSegment(sketch, "E309", {"start": v(12.24, -11.43) * mm, "end": v(12.52, -11.4) * mm});
            skLineSegment(sketch, "E310", {"start": v(12.52, -11.4) * mm, "end": v(12.6, -11.4) * mm});
            skLineSegment(sketch, "E311", {"start": v(12.6, -11.4) * mm, "end": v(12.86, -11.5) * mm});
            skLineSegment(sketch, "E312", {"start": v(12.86, -11.5) * mm, "end": v(12.98, -11.68) * mm});
            skLineSegment(sketch, "E313", {"start": v(12.98, -11.68) * mm, "end": v(12.98, -11.74) * mm});
            skLineSegment(sketch, "E314", {"start": v(12.98, -11.74) * mm, "end": v(12.98, -11.8) * mm});
            skLineSegment(sketch, "E315", {"start": v(12.98, -11.8) * mm, "end": v(12.87, -12) * mm});
            skLineSegment(sketch, "E316", {"start": v(12.87, -12) * mm, "end": v(12.63, -12.07) * mm});
            skLineSegment(sketch, "E317", {"start": v(12.63, -12.07) * mm, "end": v(12.56, -12.07) * mm});
            skLineSegment(sketch, "E318", {"start": v(12.56, -12.07) * mm, "end": v(12.48, -12.07) * mm});
            skLineSegment(sketch, "E319", {"start": v(12.48, -12.07) * mm, "end": v(12.27, -12.06) * mm});
            skLineSegment(sketch, "E320", {"start": v(12.27, -12.06) * mm, "end": v(12.25, -12.06) * mm});
            skLineSegment(sketch, "E321", {"start": v(12.25, -12.06) * mm, "end": v(12.12, -12.04) * mm});
            skLineSegment(sketch, "E322", {"start": v(12.12, -12.04) * mm, "end": v(11.3, -11.95) * mm});
            skLineSegment(sketch, "E323", {"start": v(11.3, -11.95) * mm, "end": v(11.03, -11.95) * mm});
            skLineSegment(sketch, "E324", {"start": v(11.03, -11.95) * mm, "end": v(10.77, -11.95) * mm});
            skLineSegment(sketch, "E325", {"start": v(10.77, -11.95) * mm, "end": v(10.1, -12.02) * mm});
            skLineSegment(sketch, "E326", {"start": v(10.1, -12.02) * mm, "end": v(10, -12.04) * mm});
            skLineSegment(sketch, "E327", {"start": v(10, -12.04) * mm, "end": v(9.95, -12.04) * mm});
            skLineSegment(sketch, "E328", {"start": v(9.95, -12.04) * mm, "end": v(9.62, -12.08) * mm});
            skLineSegment(sketch, "E329", {"start": v(9.62, -12.08) * mm, "end": v(9.52, -12.08) * mm});
            skLineSegment(sketch, "E330", {"start": v(9.52, -12.08) * mm, "end": v(9.44, -12.08) * mm});
            skLineSegment(sketch, "E331", {"start": v(9.44, -12.08) * mm, "end": v(9.2, -12) * mm});
            skLineSegment(sketch, "E332", {"start": v(9.2, -12) * mm, "end": v(9.1, -11.8) * mm});
            skLineSegment(sketch, "E333", {"start": v(9.1, -11.8) * mm, "end": v(9.1, -11.74) * mm});
            skLineSegment(sketch, "E334", {"start": v(9.1, -11.74) * mm, "end": v(9.1, -11.68) * mm});
            skLineSegment(sketch, "E335", {"start": v(9.1, -11.68) * mm, "end": v(9.22, -11.5) * mm});
            skLineSegment(sketch, "E336", {"start": v(9.22, -11.5) * mm, "end": v(9.49, -11.4) * mm});
            skLineSegment(sketch, "E337", {"start": v(9.49, -11.4) * mm, "end": v(9.57, -11.4) * mm});
            skLineSegment(sketch, "E338", {"start": v(9.57, -11.4) * mm, "end": v(9.65, -11.4) * mm});
            skLineSegment(sketch, "E339", {"start": v(9.65, -11.4) * mm, "end": v(9.84, -11.43) * mm});
            skLineSegment(sketch, "E340", {"start": v(9.84, -11.43) * mm, "end": v(9.87, -11.44) * mm});
            skLineSegment(sketch, "E341", {"start": v(9.87, -11.44) * mm, "end": v(9.9, -11.44) * mm});
            skLineSegment(sketch, "E342", {"start": v(9.9, -11.44) * mm, "end": v(10.1, -11.45) * mm});
            skLineSegment(sketch, "E343", {"start": v(10.1, -11.45) * mm, "end": v(10.16, -11.45) * mm});
            skLineSegment(sketch, "E344", {"start": v(10.16, -11.45) * mm, "end": v(10.26, -11.45) * mm});
            skLineSegment(sketch, "E345", {"start": v(10.26, -11.45) * mm, "end": v(10.55, -11.24) * mm});
            skLineSegment(sketch, "E346", {"start": v(10.55, -11.24) * mm, "end": v(10.57, -11.2) * mm});
            skLineSegment(sketch, "E347", {"start": v(10.57, -11.2) * mm, "end": v(10.58, -11.15) * mm});
            skLineSegment(sketch, "E348", {"start": v(10.58, -11.15) * mm, "end": v(10.62, -10.72) * mm});
            skLineSegment(sketch, "E349", {"start": v(10.62, -10.72) * mm, "end": v(10.64, -10.06) * mm});
            skLineSegment(sketch, "E350", {"start": v(10.64, -10.06) * mm, "end": v(10.64, -9.84) * mm});
            skSolve(sketch);
        }
        {
            var Q0;
            Q0 = qSketchRegion(id + "F3", true);
            var Q1;
            Q1 = qSketchRegion(id + "F4", true);
            extrude(context, id + "F5", {"entities" : qUnion([Q0, Q1]), "depth" : -3 * mm});
        }
    });
